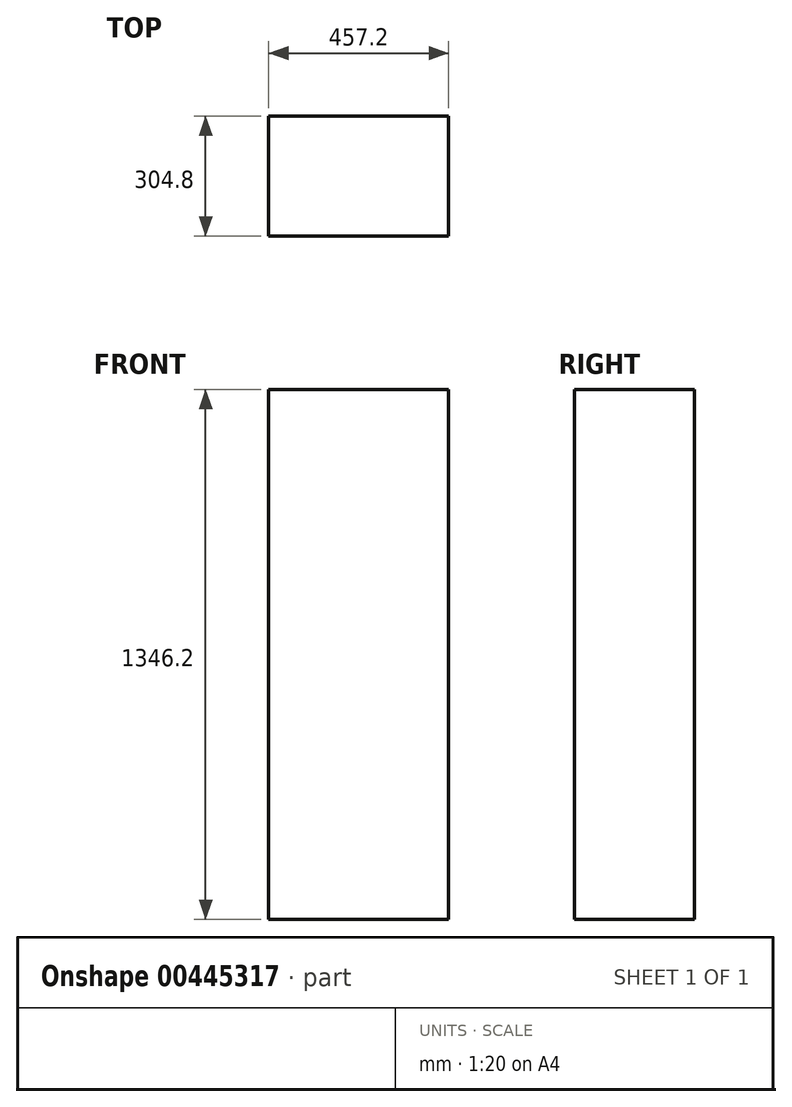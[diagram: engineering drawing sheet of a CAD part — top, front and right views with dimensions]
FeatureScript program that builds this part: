
annotation { "Feature Type Name" : "Feature", "Feature Type Description" : "" }
export const myFeature = defineFeature(function(context is Context, id is Id, definition is map)
    precondition{}
    {
        {
            var Q0;
            Q0=qCreatedBy(makeId("Front.planeOp"),FACE);
            var sketch = newSketch(context, id + "F0", { "sketchPlane" : qUnion([Q0])});
            skLineSegment(sketch, "E0.bottom", {"start": v(0, 0) * mm, "end": v(457.2, 0) * mm});
            skLineSegment(sketch, "E0.top", {"start": v(0, 1346.2) * mm, "end": v(457.2, 1346.2) * mm});
            skLineSegment(sketch, "E0.left", {"start": v(0, 0) * mm, "end": v(0, 1346.2) * mm});
            skLineSegment(sketch, "E0.right", {"start": v(457.2, 0) * mm, "end": v(457.2, 1346.2) * mm});
            skSolve(sketch);
        }
        {
            var Q0;
            Q0=makeQuery(id+"F0.imprint","IMPRINT",FACE,{"disambiguationData":[TD([[makeQuery(id+"F0.imprint","IMPRINT",EDGE,{"derivedFrom":sQuery(id+"F0.wireOp",EDGE,"E0.bottom")}),1.0]])]});
            extrude(context, id + "F1", {"entities" : qUnion([Q0]), "depth" : 304.8 * mm});
        }
    });
